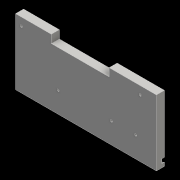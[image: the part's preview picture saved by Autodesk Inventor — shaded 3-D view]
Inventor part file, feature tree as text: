
AUTODESK INVENTOR PART (.ipt)
format: ipt  version: 2016 (Build 200138000, 138)  size: 901,120 bytes
history: native  units: mm
features: sketch x3, extrude x3, other x1, hole x1, imported_body x1
ambient origin geometry x8: Origin, YZ Plane, XZ Plane, XY Plane, X Axis, Y Axis, Z Axis, Center Point
bodies: Solid1 (feature_tree)
feature tree (9):
  sketch  "Sketch1"  dims[d6=5.4mm d7=20.0mm d9=10.0mm d10=20.0mm d12=10.0mm]
  sketch  "Sketch4"  dims[d16=20.0mm d18=20.0mm d19=5.4mm d20=10.0mm d21=10.0mm]
  other  "magnets"
  extrude  "Extrusion1"  Depth=10.0mm
  extrude  "Extrusion2"  Depth=56.0mm
  sketch  "Sketch8"  dims[d23=20.0mm d25=20.0mm d26=5.4mm d27=10.0mm d28=10.0mm d29=56.0mm d30=66.0mm d31=57.0mm d39=7.0mm d40=0.0mm d41=2.2mm d42=0.0mm d50=60.0mm d51=2.85mm d52=1.0mm d53=360.0deg d54=5.0mm d58=60.0mm d66=60.0mm d68=60.0mm d76=60.0mm d78=60.0mm d80=60.0mm d88=60.0mm d90=60.0mm d92=60.0mm d94=60.0mm d111=60.0mm d112=2.85mm d113=1.0mm d114=360.0deg d115=5.0mm d117=60.0mm d119=60.0mm d120=2.85mm d121=1.0mm d122=360.0deg d123=5.0mm d125=60.0mm d127=60.0mm d129=60.0mm d130=2.85mm d131=1.0mm d132=360.0deg d133=5.0mm d135=60.0mm d137=60.0mm d139=60.0mm d141=60.0mm d142=2.85mm d143=1.0mm d144=360.0deg d145=5.0mm d146=2.3mm d147=0.0mm d148=2.0mm d149=4.0mm d150=4.0mm d151=4.2mm d152=90.0deg d153=6.3mm d154=20.594885mm]
  extrude  "Extrusion4"  Depth=66.0mm
  hole  "Hole2"  [1 undecoded]
  imported_body  "base"
note: 1 required parameter value undecoded (feature->parameter linkage not recoverable at this tier; creation-order binding heuristic only, values carry confidence <= 0.55)
